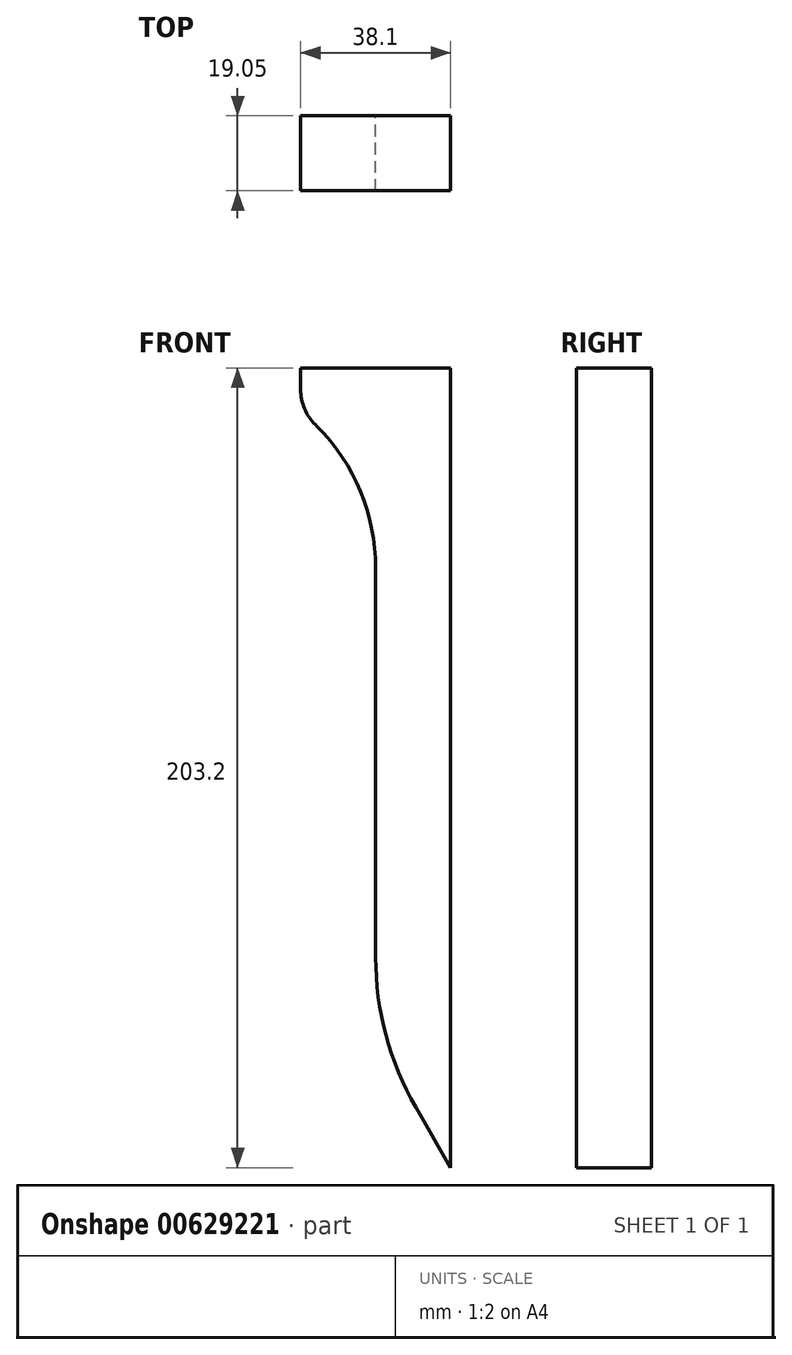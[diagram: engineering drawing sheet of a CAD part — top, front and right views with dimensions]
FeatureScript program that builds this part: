
annotation { "Feature Type Name" : "Feature", "Feature Type Description" : "" }
export const myFeature = defineFeature(function(context is Context, id is Id, definition is map)
    precondition{}
    {
        {
            var Q0;
            Q0=qCreatedBy(makeId("Front.planeOp"),FACE);
            var sketch = newSketch(context, id + "F0", { "sketchPlane" : qUnion([Q0])});
            skLineSegment(sketch, "E0", {"start": v(0, 0) * mm, "end": v(-8.84, 15.31) * mm});
            skLineSegment(sketch, "E1", {"start": v(-19.05, 53.41) * mm, "end": v(-19.05, 152.4) * mm});
            skLineSegment(sketch, "E2", {"start": v(-33.93, 188.32) * mm, "end": v(-34.38, 188.77) * mm});
            skLineSegment(sketch, "E3", {"start": v(-38.1, 197.75) * mm, "end": v(-38.1, 203.2) * mm});
            skLineSegment(sketch, "E4", {"start": v(-38.1, 203.2) * mm, "end": v(0, 203.2) * mm});
            skLineSegment(sketch, "E5", {"start": v(0, 203.2) * mm, "end": v(0, 0) * mm});
            skPoint(sketch, "E6.visualSharp", {"position": v(-19.05, 33) * mm});
            skArc(sketch, "E6.filletArc", {"start": v(-19.05, 53.41) * mm, "mid": v(-16.45, 33.7) * mm, "end": v(-8.84, 15.31) * mm});
            skPoint(sketch, "E7.visualSharp", {"position": v(-19.05, 173.44) * mm});
            skArc(sketch, "E7.filletArc", {"start": v(-19.05, 152.4) * mm, "mid": v(-22.92, 171.84) * mm, "end": v(-33.93, 188.32) * mm});
            skPoint(sketch, "E8.visualSharp", {"position": v(-38.1, 192.5) * mm});
            skArc(sketch, "E8.filletArc", {"start": v(-38.1, 197.75) * mm, "mid": v(-37.13, 192.9) * mm, "end": v(-34.38, 188.77) * mm});
            skSolve(sketch);
        }
        {
            var Q0;
            Q0=makeQuery(id+"F0.imprint","IMPRINT",FACE,{"disambiguationData":[TD([[makeQuery(id+"F0.imprint","IMPRINT",EDGE,{"derivedFrom":sQuery(id+"F0.wireOp",EDGE,"E0")}),-1.0]])]});
            extrude(context, id + "F1", {"entities" : qUnion([Q0]), "depth" : 19.05 * mm, "offsetDistance" : 25.4 * mm});
        }
    });
